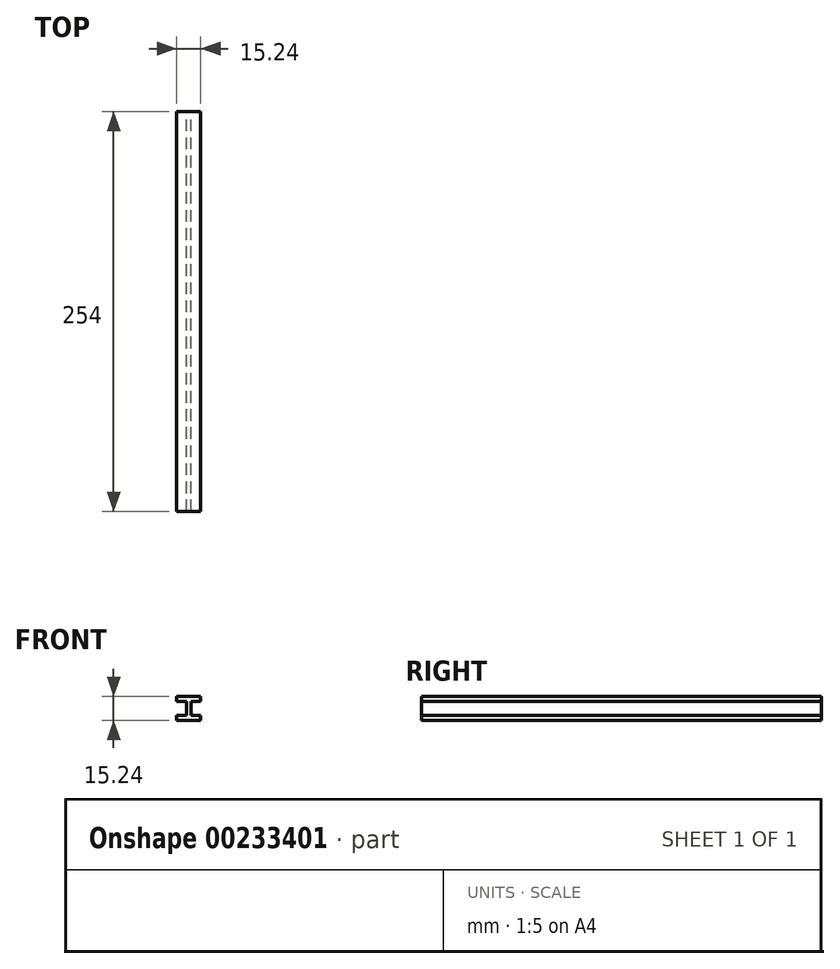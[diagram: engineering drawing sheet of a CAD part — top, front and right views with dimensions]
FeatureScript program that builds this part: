
annotation { "Feature Type Name" : "Feature", "Feature Type Description" : "" }
export const myFeature = defineFeature(function(context is Context, id is Id, definition is map)
    precondition{}
    {
        {
            var Q0;
            Q0=qCreatedBy(makeId("Front.planeOp"),FACE);
            var sketch = newSketch(context, id + "F0", { "sketchPlane" : qUnion([Q0])});
            skLineSegment(sketch, "E0", {"start": v(0, 0) * mm, "end": v(-1.52, 0) * mm});
            skLineSegment(sketch, "E1", {"start": v(-1.52, 0) * mm, "end": v(-1.52, 4.57) * mm});
            skLineSegment(sketch, "E2", {"start": v(-1.52, 4.57) * mm, "end": v(-7.62, 4.57) * mm});
            skLineSegment(sketch, "E3", {"start": v(-7.62, 4.57) * mm, "end": v(-7.62, 7.62) * mm});
            skLineSegment(sketch, "E4", {"start": v(-7.62, 7.62) * mm, "end": v(0, 7.62) * mm});
            skLineSegment(sketch, "E5", {"start": v(0, 7.62) * mm, "end": v(0, 0) * mm});
            skSolve(sketch);
        }
        {
            var Q0;
            Q0 = qSketchRegion(id + "F0", true);
            extrude(context, id + "F1", {"entities" : qUnion([Q0]), "depth" : 254 * mm});
        }
        {
            var Q0;
            Q0=makeQuery(id+"F1.opExtrude","SWEPT_BODY",BODY,{"disambiguationData":[OSD([sQuery(id+"F0.wireOp",EDGE,"E0"),sQuery(id+"F0.wireOp",EDGE,"E1"),sQuery(id+"F0.wireOp",EDGE,"E2"),sQuery(id+"F0.wireOp",EDGE,"E3"),sQuery(id+"F0.wireOp",EDGE,"E4"),sQuery(id+"F0.wireOp",EDGE,"E5")])]});
            var Q1;
            Q1=makeQuery(id+"F1.opExtrude","SWEPT_FACE",FACE,{"disambiguationData":[OSD([sQuery(id+"F0.wireOp",EDGE,"E5")])]});
            mirror(context, id + "F2", {"operationType" : NewBodyOperationType.ADD, "entities" : qUnion([Q0]), "mirrorPlane" : qUnion([Q1])});
        }
        {
            var Q0;
            Q0=makeQuery(id+"F1.opExtrude","SWEPT_BODY",BODY,{"disambiguationData":[OSD([sQuery(id+"F0.wireOp",EDGE,"E0"),sQuery(id+"F0.wireOp",EDGE,"E1"),sQuery(id+"F0.wireOp",EDGE,"E2"),sQuery(id+"F0.wireOp",EDGE,"E3"),sQuery(id+"F0.wireOp",EDGE,"E4"),sQuery(id+"F0.wireOp",EDGE,"E5")])]});
            var Q1;
            {var subQ0=makeQuery(id+"F1.opExtrude","SWEPT_FACE",FACE,{"disambiguationData":[OSD([sQuery(id+"F0.wireOp",EDGE,"E0")])]});Q1=makeQuery(id+"F2.boolean.opBoolean","MERGE",FACE,{"derivedFrom":[subQ0,makeQuery(id+"F2.opPattern","COPY",FACE,{"derivedFrom":subQ0,"instanceName":"1"})]});}
            mirror(context, id + "F3", {"operationType" : NewBodyOperationType.ADD, "entities" : qUnion([Q0]), "mirrorPlane" : qUnion([Q1])});
        }
    });
